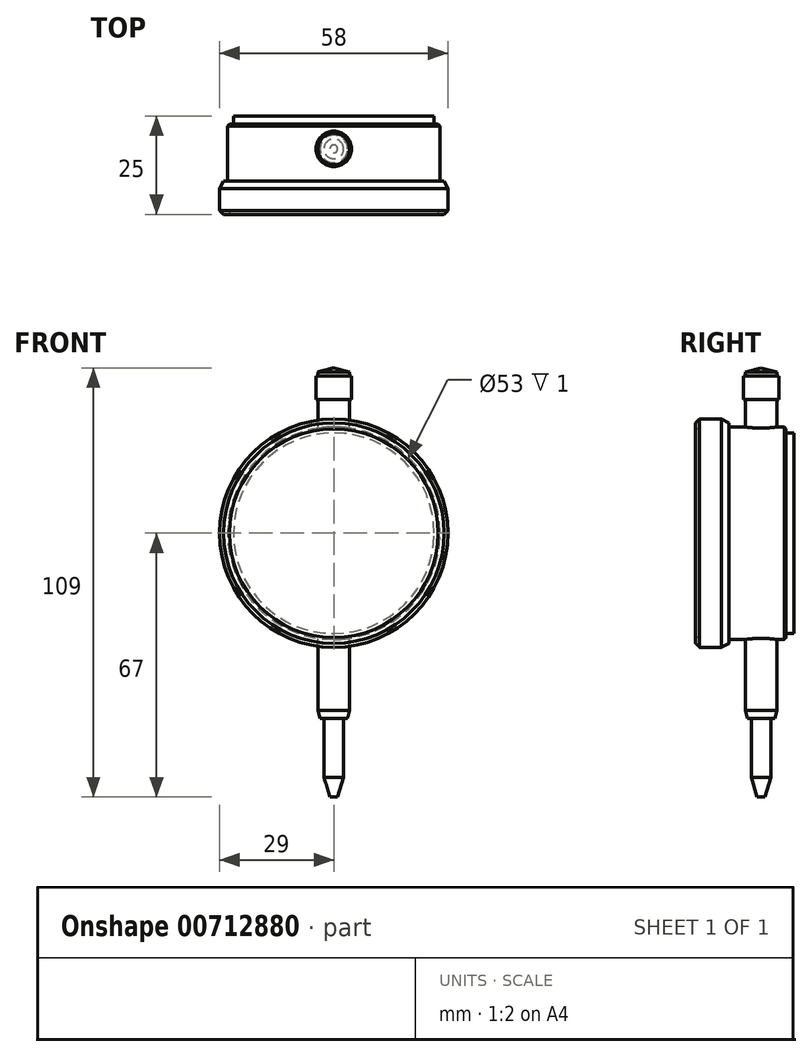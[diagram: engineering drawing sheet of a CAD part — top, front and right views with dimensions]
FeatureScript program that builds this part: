
annotation { "Feature Type Name" : "Feature", "Feature Type Description" : "" }
export const myFeature = defineFeature(function(context is Context, id is Id, definition is map)
    precondition{}
    {
        {
            var Q0;
            Q0=qCreatedBy(makeId("Front.planeOp"),FACE);
            var sketch = newSketch(context, id + "F0", { "sketchPlane" : qUnion([Q0])});
            skCircle(sketch, "E0", {"center": v(0, 0) * mm, "radius": 25.5 * mm});
            skSolve(sketch);
        }
        {
            var Q0;
            Q0=qSketchRegion(id+"F0",true);
            extrude(context, id + "F1", {"entities" : qUnion([Q0]), "depth" : 2 * mm, "offsetDistance" : 25 * mm});
        }
        {
            var Q0;
            Q0=makeQuery(id+"F1.opExtrude","CAP_FACE",FACE,{"disambiguationData":[OSD([sQuery(id+"F0.wireOp",EDGE,"E0")])],"isStart":false});
            var sketch = newSketch(context, id + "F2", { "sketchPlane" : qUnion([Q0])});
            skCircle(sketch, "E1", {"center": v(0, 0) * mm, "radius": 27 * mm});
            skSolve(sketch);
        }
        {
            var Q0;
            Q0=qSketchRegion(id+"F2",true);
            extrude(context, id + "F3", {"entities" : qUnion([Q0]), "operationType" : NewBodyOperationType.ADD, "depth" : 14.5 * mm, "offsetDistance" : 25 * mm});
        }
        {
            var Q0;
            Q0=makeQuery(id+"F3.opExtrude","CAP_FACE",FACE,{"disambiguationData":[OSD([sQuery(id+"F2.wireOp",EDGE,"E1")])],"isStart":false});
            var sketch = newSketch(context, id + "F4", { "sketchPlane" : qUnion([Q0])});
            skCircle(sketch, "E2", {"center": v(0, 0) * mm, "radius": 29 * mm});
            skSolve(sketch);
        }
        {
            var Q0;
            Q0=qSketchRegion(id+"F4",true);
            extrude(context, id + "F5", {"entities" : qUnion([Q0]), "operationType" : NewBodyOperationType.ADD, "depth" : 8.5 * mm, "offsetDistance" : 25 * mm});
        }
        {
            var Q0;
            Q0=qCreatedBy(makeId("Top.planeOp"),FACE);
            var sketch = newSketch(context, id + "F6", { "sketchPlane" : qUnion([Q0])});
            skCircle(sketch, "E3", {"center": v(0, -8.36) * mm, "radius": 4 * mm});
            skSolve(sketch);
        }
        {
            var Q0;
            Q0=qSketchRegion(id+"F6",true);
            extrude(context, id + "F7", {"entities" : qUnion([Q0]), "operationType" : NewBodyOperationType.ADD, "oppositeDirection" : true, "depth" : 47 * mm, "offsetDistance" : 25 * mm, "hasSecondDirection" : true, "secondDirectionOppositeDirection" : false, "secondDirectionDepth" : 34 * mm});
        }
        {
            var Q0;
            Q0=makeQuery(id+"F7.opExtrude","CAP_FACE",FACE,{"disambiguationData":[OSD([sQuery(id+"F6.wireOp",EDGE,"E3")])],"isStart":false});
            var sketch = newSketch(context, id + "F8", { "sketchPlane" : qUnion([Q0])});
            skCircle(sketch, "E4", {"center": v(0, 8.36) * mm, "radius": 2.5 * mm});
            skSolve(sketch);
        }
        {
            var Q0;
            Q0=qSketchRegion(id+"F8",true);
            extrude(context, id + "F9", {"entities" : qUnion([Q0]), "operationType" : NewBodyOperationType.ADD, "depth" : 20 * mm, "offsetDistance" : 25 * mm});
        }
        {
            var Q0;
            Q0=makeQuery(id+"F7.opExtrude","CAP_FACE",FACE,{"disambiguationData":[OSD([sQuery(id+"F6.wireOp",EDGE,"E3")])],"isStart":true});
            var sketch = newSketch(context, id + "F10", { "sketchPlane" : qUnion([Q0])});
            skCircle(sketch, "E5", {"center": v(0, -8.36) * mm, "radius": 4.5 * mm});
            skSolve(sketch);
        }
        {
            var Q0;
            Q0=qSketchRegion(id+"F10",true);
            extrude(context, id + "F11", {"entities" : qUnion([Q0]), "operationType" : NewBodyOperationType.ADD, "depth" : 6 * mm, "offsetDistance" : 25 * mm});
        }
        {
            var Q0;
            Q0=makeQuery(id+"F11.opExtrude","CAP_FACE",FACE,{"disambiguationData":[OSD([sQuery(id+"F10.wireOp",EDGE,"E5")])],"isStart":false});
            var sketch = newSketch(context, id + "F12", { "sketchPlane" : qUnion([Q0])});
            skCircle(sketch, "E6", {"center": v(0, -8.36) * mm, "radius": 4 * mm});
            skSolve(sketch);
        }
        {
            var Q0;
            Q0=qSketchRegion(id+"F12",true);
            extrude(context, id + "F13", {"entities" : qUnion([Q0]), "operationType" : NewBodyOperationType.ADD, "depth" : 2 * mm, "offsetDistance" : 25 * mm});
        }
        {
            var Q0;
            Q0=makeQuery(id+"F5.opExtrude","CAP_FACE",FACE,{"disambiguationData":[OSD([sQuery(id+"F4.wireOp",EDGE,"E2")])],"isStart":false});
            var sketch = newSketch(context, id + "F14", { "sketchPlane" : qUnion([Q0])});
            skCircle(sketch, "E7", {"center": v(0, 0) * mm, "radius": 26.5 * mm});
            skSolve(sketch);
        }
        {
            var Q0;
            Q0=qSketchRegion(id+"F14",true);
            extrude(context, id + "F15", {"entities" : qUnion([Q0]), "operationType" : NewBodyOperationType.REMOVE, "oppositeDirection" : true, "depth" : 1 * mm, "offsetDistance" : 25 * mm});
        }
        {
            var Q0;
            Q0=makeQuery(id+"F9.opExtrude","CAP_EDGE",EDGE,{"disambiguationData":[OSD([sQuery(id+"F8.wireOp",EDGE,"E4")])],"isStart":false});
            chamfer(context, id + "F16", {"entities" : qUnion([Q0]), "chamferType" : ChamferType.TWO_OFFSETS, "width1" : 1.5 * mm, "oppositeDirection" : false, "width2" : 5 * mm, "tangentPropagation" : true});
        }
        {
            var Q0;
            Q0=makeQuery(id+"F7.opExtrude","CAP_EDGE",EDGE,{"disambiguationData":[OSD([sQuery(id+"F6.wireOp",EDGE,"E3")])],"isStart":false});
            chamfer(context, id + "F17", {"entities" : qUnion([Q0]), "chamferType" : ChamferType.TWO_OFFSETS, "width1" : 0.5 * mm, "oppositeDirection" : true, "width2" : 2 * mm, "tangentPropagation" : true});
        }
        {
            var Q0;
            Q0=makeQuery(id+"F3.opExtrude","CAP_EDGE",EDGE,{"disambiguationData":[OSD([sQuery(id+"F2.wireOp",EDGE,"E1")])],"isStart":true});
            chamfer(context, id + "F18", {"entities" : qUnion([Q0]), "width" : 0.5 * mm, "tangentPropagation" : true});
        }
        {
            var Q0;
            Q0=makeQuery(id+"F5.opExtrude","CAP_EDGE",EDGE,{"disambiguationData":[OSD([sQuery(id+"F4.wireOp",EDGE,"E2")])],"isStart":false});
            chamfer(context, id + "F19", {"entities" : qUnion([Q0]), "width" : 1 * mm, "tangentPropagation" : true});
        }
        {
            var Q0;
            Q0=makeQuery(id+"F5.opExtrude","CAP_EDGE",EDGE,{"disambiguationData":[OSD([sQuery(id+"F4.wireOp",EDGE,"E2")])],"isStart":true});
            chamfer(context, id + "F20", {"entities" : qUnion([Q0]), "chamferType" : ChamferType.TWO_OFFSETS, "width1" : 2 * mm, "oppositeDirection" : false, "width2" : 1 * mm, "tangentPropagation" : true});
        }
        {
            var Q0;
            Q0=makeQuery(id+"F13.opExtrude","CAP_EDGE",EDGE,{"disambiguationData":[OSD([sQuery(id+"F12.wireOp",EDGE,"E6")])],"isStart":false});
            chamfer(context, id + "F21", {"entities" : qUnion([Q0]), "chamferType" : ChamferType.TWO_OFFSETS, "width1" : 1 * mm, "oppositeDirection" : true, "width2" : 4 * mm, "tangentPropagation" : true});
        }
    });
